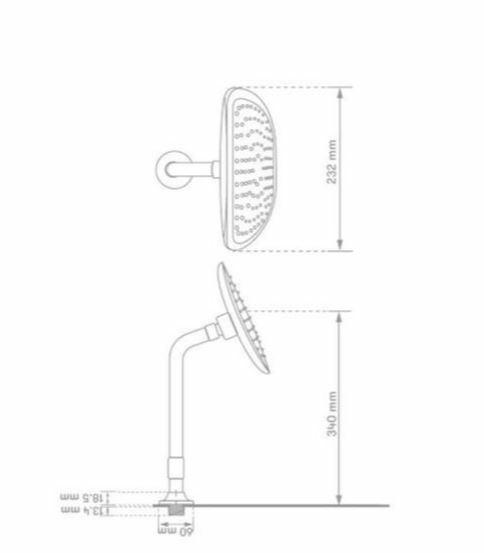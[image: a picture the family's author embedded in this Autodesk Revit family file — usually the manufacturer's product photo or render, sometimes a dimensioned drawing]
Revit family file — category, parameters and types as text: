
# Revit family: BL-8430-11-REGADERA CALIMA 3 FUNCIONES
name_source: partatom
category: Plumbing Fixtures
revit_build: Autodesk Revit 2018 (Build: 20170223_1515(x64)
units: mm (PartAtom-declared; Revit-internal decimal feet)

## family parameters
Cut with Voids When Loaded = No
Host = Face
OmniClass Number = 23.31.11.00
Part Type = Normal
Room Calculation Point = No
Round Connector Dimension = Use Diameter
Shared = No

## types (1)
- BL-8430-11
    Alto = 100 mm  [stored 0.328084 ft]
    Ancho = 100 mm  [stored 0.328084 ft]
    CW Connection = Yes
    Default Elevation = 0 mm  [stored 0 ft]
    Description = Regadera
    HW Connection = Yes
    Link Ficha Tecnica = http://infotecnica.gricol.com
    Manufacturer = Gricol
    Model = BL-8430-11
    Plastico ABS Cromado = Plastico ABS Cromado
    Product Name = REGADERA CALIMA CROMADA TRES FUNCIONES
    Profundidad = 210 mm  [stored 0.688976 ft]
    Type Image = REGADERA ISEO CUADRADA FOTO.JPG
    URL = https://www.gricol.com
    Vent Connection = No
    Waste Connection = No

note: [stored X ft] marks values corroborated as IEEE doubles in the binary element streams (Revit-internal decimal feet)

## geometry (parser evidence)
native form markers: Blend x2, Sweep x4
no freeform markers — native parametric forms only
